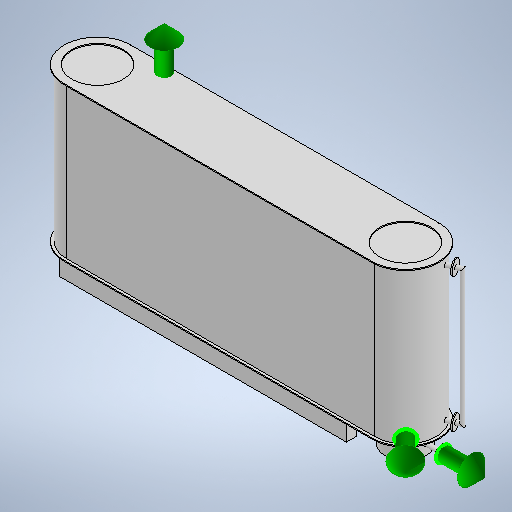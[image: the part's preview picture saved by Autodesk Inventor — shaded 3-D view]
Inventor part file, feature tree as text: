
AUTODESK INVENTOR PART (.ipt)
format: ipt  version: 2025 (Build 290162010, 162A)  size: 391,680 bytes
history: native  units: mm
features: sketch x16, extrude x13, projected_geometry x8, plane x4, sweep x1
ambient origin geometry x8: Origin, YZ Plane, XZ Plane, XY Plane, X Axis, Y Axis, Z Axis, Center Point
bodies: Solid1 (feature_tree)
feature tree (42):
  extrude  "Extrusion1"  Depth=600.0mm
  extrude  "Extrusion2"  Depth=25.0mm
  extrude  "Extrusion3"  Depth=25.0mm
  extrude  "Extrusion4"  Depth=10.0mm
  plane  "Work Plane1"
  extrude  "Extrusion5"  Depth=200.0mm
  extrude  "Extrusion6"  Depth=100.0mm TaperAngle=0.0deg
  sketch  "Sketch7"  dims[d18=145.0mm d19=10.0mm d20=0.0mm]
  plane  "Work Plane2"
  plane  "Work Plane3"
  extrude  "Extrusion7"  Depth=10.0mm TaperAngle=0.0deg
  extrude  "Extrusion8"  TaperAngle=45.0deg  [1 undecoded]
  extrude  "Extrusion9"  Depth=100.0mm TaperAngle=0.0deg
  extrude  "Extrusion10"  Depth=100.0mm TaperAngle=0.0deg
  extrude  "Extrusion11"  Depth=10.0mm TaperAngle=0.0deg
  extrude  "Extrusion12"  Depth=135.0mm
  extrude  "Extrusion13"  Depth=10.0mm TaperAngle=0.0deg
  sketch  "Sketch19"  dims[d50=10.0mm d51=0.0mm]
  plane  "Work Plane7"
  sweep  "Sweep1"
  sketch  "Sketch1"  dims[d0=3000.0mm d1=600.0mm]
  sketch  "Sketch2"  dims[d2=1500.0mm d3=0.0mm d4=25.0mm]
  projected_geometry  "Projected Loop1"
  sketch  "Sketch3"  dims[d5=10.0mm d6=0.0mm d7=25.0mm]
  projected_geometry  "Projected Loop2"
  sketch  "Sketch4"  dims[d8=10.0mm d9=0.0mm d10=400.0mm]
  sketch  "Sketch5"  dims[d11=200.0mm d12=0.0mm d13=40.0mm]
  projected_geometry  "Projected Loop3"
  projected_geometry  "Projected Loop4"
  sketch  "Sketch6"  dims[d14=100.0mm d15=365.0mm d16=0.0mm]
  projected_geometry  "Projected Loop5"
  projected_geometry  "Projected Loop6"
  sketch  "Sketch8"  dims[d21=22.5deg d23=45.0deg]
  projected_geometry  "Projected Loop7"
  sketch  "Sketch9"  dims[d24=40.0mm d27=50.0mm d28=100.0mm d29=0.0mm d30=0.0mm]
  projected_geometry  "Projected Loop8"
  sketch  "Sketch10"  dims[d31=63.0mm d33=50.0mm d34=100.0mm d35=0.0mm d36=0.0mm]
  sketch  "Sketch13"  dims[d37=160.0mm d38=10.0mm d39=0.0mm]
  sketch  "Sketch14"  dims[d40=172.5mm d44=135.0mm]
  sketch  "Sketch15"  dims[d45=135.0mm d46=10.0mm d47=0.0mm]
  sketch  "Sketch16"  dims[d48=500.0mm d49=500.0mm]
  sketch  "Sketch20"  dims[d52=100.0mm d53=550.0mm d55=200.0mm d56=0.0mm d59=1200.0mm d60=1600.0mm d62=50.0mm d63=1100.0mm d64=250.0mm d65=10.0mm d66=0.0mm d68=50.0mm d69=0.0mm d70=0.0mm d71=0.0mm]
note: 1 required parameter value undecoded (feature->parameter linkage not recoverable at this tier; creation-order binding heuristic only, values carry confidence <= 0.55)
